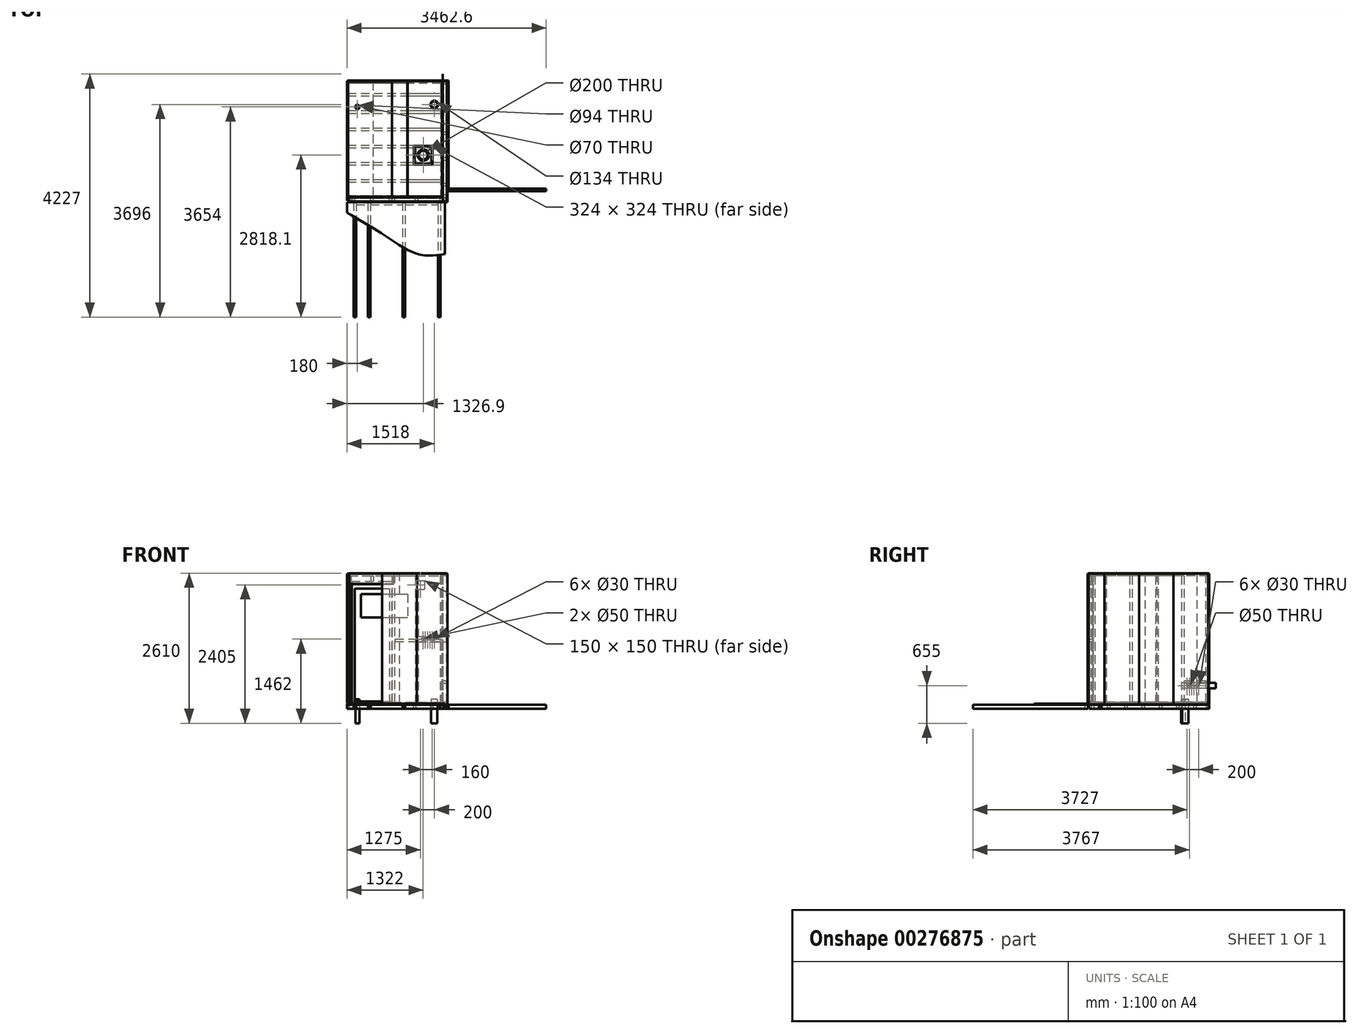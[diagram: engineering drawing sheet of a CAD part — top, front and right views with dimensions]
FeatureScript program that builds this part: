
annotation { "Feature Type Name" : "Feature", "Feature Type Description" : "" }
export const myFeature = defineFeature(function(context is Context, id is Id, definition is map)
    precondition{}
    {
        {
            var Q0;
            Q0=qCreatedBy(makeId("Front.planeOp"),FACE);
            cPlane(context, id + "F0", {"entities" : qUnion([Q0]), "cplaneType" : CPlaneType.OFFSET, "offset" : 15 * mm, "oppositeDirection" : true, "width" : 150 * mm, "height" : 150 * mm});
        }
        {
            var Q0;
            Q0=qCreatedBy(makeId("Right.planeOp"),FACE);
            cPlane(context, id + "F1", {"entities" : qUnion([Q0]), "cplaneType" : CPlaneType.OFFSET, "offset" : (15 + 20) * mm, "oppositeDirection" : true, "width" : 150 * mm, "height" : 150 * mm});
        }
        {
            var Q0;
            Q0=qCreatedBy(id+"F1.planeOp",FACE);
            cPlane(context, id + "F2", {"entities" : qUnion([Q0]), "cplaneType" : CPlaneType.OFFSET, "offset" : 1700 * mm, "width" : 150 * mm, "height" : 150 * mm});
        }
        {
            var Q0;
            Q0=qCreatedBy(id+"F0.planeOp",FACE);
            cPlane(context, id + "F3", {"entities" : qUnion([Q0]), "cplaneType" : CPlaneType.OFFSET, "offset" : 2069 * mm, "width" : 150 * mm, "height" : 150 * mm});
        }
        {
            var Q0;
            Q0=qCreatedBy(makeId("Top.planeOp"),FACE);
            cPlane(context, id + "F4", {"entities" : qUnion([Q0]), "cplaneType" : CPlaneType.OFFSET, "offset" : 0 * mm, "width" : 150 * mm, "height" : 150 * mm});
        }
        {
            var Q0;
            Q0=qCreatedBy(id+"F4.planeOp",FACE);
            var sketch = newSketch(context, id + "F5", { "sketchPlane" : qUnion([Q0])});
            skLineSegment(sketch, "E0.bottom", {"start": v(80, -2099) * mm, "end": v(125, -2099) * mm});
            skLineSegment(sketch, "E0.top", {"start": v(80, -4099) * mm, "end": v(125, -4099) * mm});
            skLineSegment(sketch, "E0.left", {"start": v(80, -2099) * mm, "end": v(80, -4099) * mm});
            skLineSegment(sketch, "E0.right", {"start": v(125, -2099) * mm, "end": v(125, -4099) * mm});
            skLineSegment(sketch, "E1.bottom", {"start": v(330, -2099) * mm, "end": v(375, -2099) * mm});
            skLineSegment(sketch, "E1.top", {"start": v(330, -4099) * mm, "end": v(375, -4099) * mm});
            skLineSegment(sketch, "E1.left", {"start": v(330, -2099) * mm, "end": v(330, -4099) * mm});
            skLineSegment(sketch, "E1.right", {"start": v(375, -2099) * mm, "end": v(375, -4099) * mm});
            skLineSegment(sketch, "E2.bottom", {"start": v(930, -2099) * mm, "end": v(975, -2099) * mm});
            skLineSegment(sketch, "E2.top", {"start": v(930, -4099) * mm, "end": v(975, -4099) * mm});
            skLineSegment(sketch, "E2.left", {"start": v(930, -2099) * mm, "end": v(930, -4099) * mm});
            skLineSegment(sketch, "E2.right", {"start": v(975, -2099) * mm, "end": v(975, -4099) * mm});
            skLineSegment(sketch, "E3.bottom", {"start": v(1545, -2099) * mm, "end": v(1590, -2099) * mm});
            skLineSegment(sketch, "E3.top", {"start": v(1545, -4099) * mm, "end": v(1590, -4099) * mm});
            skLineSegment(sketch, "E3.left", {"start": v(1545, -2099) * mm, "end": v(1545, -4099) * mm});
            skLineSegment(sketch, "E3.right", {"start": v(1590, -2099) * mm, "end": v(1590, -4099) * mm});
            skLineSegment(sketch, "E4.bottom", {"start": v(0, 0) * mm, "end": v(10, 0) * mm});
            skLineSegment(sketch, "E4.top", {"start": v(0, -10) * mm, "end": v(10, -10) * mm});
            skLineSegment(sketch, "E4.left", {"start": v(0, 0) * mm, "end": v(0, -10) * mm});
            skLineSegment(sketch, "E4.right", {"start": v(10, 0) * mm, "end": v(10, -10) * mm});
            skSolve(sketch);
        }
        {
            var Q0;
            Q0 = qSketchRegion(id + "F5", true);
            extrude(context, id + "F6", {"entities" : qUnion([Q0]), "oppositeDirection" : true, "depth" : 70 * mm});
        }
        {
            var Q0;
            Q0=qCreatedBy(id+"F4.planeOp",FACE);
            var sketch = newSketch(context, id + "F7", { "sketchPlane" : qUnion([Q0])});
            skLineSegment(sketch, "E5.bottom", {"start": v(-35, -2099) * mm, "end": v(1665, -2099) * mm});
            skLineSegment(sketch, "E5.left", {"start": v(-35, -2099) * mm, "end": v(-35, -2282.36) * mm});
            skLineSegment(sketch, "E5.right", {"start": v(1665, -2099) * mm, "end": v(1665, -3003.52) * mm});
            skFitSpline(sketch, "E6", {"points": [v(-35, -2282.36) * mm, v(571.63, -2645.47) * mm, v(1201.22, -3003.52) * mm, v(1665, -3003.52) * mm], "startDerivative": vector(1648.34, -970.88) * mm, "endDerivative": vector(1571.62, 233.74) * mm});
            skSolve(sketch);
        }
        {
            var Q0;
            Q0 = qSketchRegion(id + "F7", true);
            extrude(context, id + "F8", {"entities" : qUnion([Q0]), "depth" : 22 * mm});
        }
        {
            var Q0;
            Q0=qCreatedBy(id+"F4.planeOp",FACE);
            var sketch = newSketch(context, id + "F9", { "sketchPlane" : qUnion([Q0])});
            skLineSegment(sketch, "E7.bottom", {"start": v(1687.5, 15) * mm, "end": v(1642.5, 15) * mm});
            skLineSegment(sketch, "E7.top", {"start": v(1687.5, -2076.5) * mm, "end": v(1642.5, -2076.5) * mm});
            skLineSegment(sketch, "E7.left", {"start": v(1687.5, 15) * mm, "end": v(1687.5, -2076.5) * mm});
            skLineSegment(sketch, "E7.right", {"start": v(1642.5, 15) * mm, "end": v(1642.5, -2076.5) * mm});
            skLineSegment(sketch, "E8.bottom", {"start": v(-35, -2076.5) * mm, "end": v(1641.5, -2076.5) * mm});
            skLineSegment(sketch, "E8.top", {"start": v(-35, -2031.5) * mm, "end": v(1641.5, -2031.5) * mm});
            skLineSegment(sketch, "E8.left", {"start": v(-35, -2076.5) * mm, "end": v(-35, -2031.5) * mm});
            skLineSegment(sketch, "E8.right", {"start": v(1641.5, -2076.5) * mm, "end": v(1641.5, -2031.5) * mm});
            skPoint(sketch, "E9", {"position": v(1665, -2076.5) * mm});
            skPoint(sketch, "E10", {"position": v(1641.5, -2054) * mm});
            skLineSegment(sketch, "E11.bottom", {"start": v(126, -2099) * mm, "end": v(329, -2099) * mm});
            skLineSegment(sketch, "E11.top", {"start": v(126, -2144) * mm, "end": v(329, -2144) * mm});
            skLineSegment(sketch, "E11.left", {"start": v(126, -2099) * mm, "end": v(126, -2144) * mm});
            skLineSegment(sketch, "E11.right", {"start": v(329, -2099) * mm, "end": v(329, -2144) * mm});
            skLineSegment(sketch, "E12.bottom", {"start": v(376, -2099) * mm, "end": v(929, -2099) * mm});
            skLineSegment(sketch, "E12.top", {"start": v(376, -2144) * mm, "end": v(929, -2144) * mm});
            skLineSegment(sketch, "E12.left", {"start": v(376, -2099) * mm, "end": v(376, -2144) * mm});
            skLineSegment(sketch, "E12.right", {"start": v(929, -2099) * mm, "end": v(929, -2144) * mm});
            skLineSegment(sketch, "E13.bottom", {"start": v(976, -2099) * mm, "end": v(1544, -2099) * mm});
            skLineSegment(sketch, "E13.top", {"start": v(976, -2144) * mm, "end": v(1544, -2144) * mm});
            skLineSegment(sketch, "E13.left", {"start": v(976, -2099) * mm, "end": v(976, -2144) * mm});
            skLineSegment(sketch, "E13.right", {"start": v(1544, -2099) * mm, "end": v(1544, -2144) * mm});
            skLineSegment(sketch, "E14.bottom", {"start": v(1642.4, -2031.4) * mm, "end": v(1597.4, -2031.4) * mm});
            skLineSegment(sketch, "E14.top", {"start": v(1642.4, 15) * mm, "end": v(1597.4, 15) * mm});
            skLineSegment(sketch, "E14.left", {"start": v(1642.4, -2031.4) * mm, "end": v(1642.4, 15) * mm});
            skLineSegment(sketch, "E14.right", {"start": v(1597.4, -2031.4) * mm, "end": v(1597.4, 15) * mm});
            skLineSegment(sketch, "E15.bottom", {"start": v(-35, -1986.4) * mm, "end": v(1597.3, -1986.4) * mm});
            skLineSegment(sketch, "E15.top", {"start": v(-35, -2031.4) * mm, "end": v(1597.3, -2031.4) * mm});
            skLineSegment(sketch, "E15.left", {"start": v(-35, -1986.4) * mm, "end": v(-35, -2031.4) * mm});
            skLineSegment(sketch, "E15.right", {"start": v(1597.3, -1986.4) * mm, "end": v(1597.3, -2031.4) * mm});
            skLineSegment(sketch, "E16.bottom", {"start": v(1732.6, 15) * mm, "end": v(1687.6, 15) * mm});
            skLineSegment(sketch, "E16.top", {"start": v(1732.6, -1885) * mm, "end": v(1687.6, -1885) * mm});
            skLineSegment(sketch, "E16.left", {"start": v(1732.6, 15) * mm, "end": v(1732.6, -1885) * mm});
            skLineSegment(sketch, "E16.right", {"start": v(1687.6, 15) * mm, "end": v(1687.6, -1885) * mm});
            skLineSegment(sketch, "E17.bottom", {"start": v(1732.7, -1863) * mm, "end": v(3427.6, -1863) * mm});
            skLineSegment(sketch, "E17.top", {"start": v(1732.7, -1908) * mm, "end": v(3427.6, -1908) * mm});
            skLineSegment(sketch, "E17.left", {"start": v(1732.7, -1863) * mm, "end": v(1732.7, -1908) * mm});
            skLineSegment(sketch, "E17.right", {"start": v(3427.6, -1863) * mm, "end": v(3427.6, -1908) * mm});
            skSolve(sketch);
        }
        {
            var Q0;
            Q0 = qSketchRegion(id + "F9", true);
            extrude(context, id + "F10", {"entities" : qUnion([Q0]), "oppositeDirection" : true, "depth" : 70 * mm});
        }
        {
            var Q0;
            Q0=qCreatedBy(id+"F4.planeOp",FACE);
            var sketch = newSketch(context, id + "F11", { "sketchPlane" : qUnion([Q0])});
            skLineSegment(sketch, "E18.bottom", {"start": v(-25, -1708.4) * mm, "end": v(1596.4, -1708.4) * mm});
            skLineSegment(sketch, "E18.top", {"start": v(-25, -1753.4) * mm, "end": v(1596.4, -1753.4) * mm});
            skLineSegment(sketch, "E18.left", {"start": v(-25, -1708.4) * mm, "end": v(-25, -1753.4) * mm});
            skLineSegment(sketch, "E18.right", {"start": v(1596.4, -1708.4) * mm, "end": v(1596.4, -1753.4) * mm});
            skLineSegment(sketch, "E19.0.1.0", {"start": v(-25, -1408.4) * mm, "end": v(-25, -1453.4) * mm});
            skLineSegment(sketch, "E19.0.1.1", {"start": v(-25, -1408.4) * mm, "end": v(1596.4, -1408.4) * mm});
            skLineSegment(sketch, "E19.0.1.2", {"start": v(-25, -1453.4) * mm, "end": v(1596.4, -1453.4) * mm});
            skLineSegment(sketch, "E19.0.1.3", {"start": v(1596.4, -1408.4) * mm, "end": v(1596.4, -1453.4) * mm});
            skLineSegment(sketch, "E19.0.2.0", {"start": v(-25, -1108.4) * mm, "end": v(-25, -1153.4) * mm});
            skLineSegment(sketch, "E19.0.2.1", {"start": v(-25, -1108.4) * mm, "end": v(1596.4, -1108.4) * mm});
            skLineSegment(sketch, "E19.0.2.2", {"start": v(-25, -1153.4) * mm, "end": v(1596.4, -1153.4) * mm});
            skLineSegment(sketch, "E19.0.2.3", {"start": v(1596.4, -1108.4) * mm, "end": v(1596.4, -1153.4) * mm});
            skLineSegment(sketch, "E19.0.3.0", {"start": v(-25, -808.4) * mm, "end": v(-25, -853.4) * mm});
            skLineSegment(sketch, "E19.0.3.1", {"start": v(-25, -808.4) * mm, "end": v(1596.4, -808.4) * mm});
            skLineSegment(sketch, "E19.0.3.2", {"start": v(-25, -853.4) * mm, "end": v(1596.4, -853.4) * mm});
            skLineSegment(sketch, "E19.0.3.3", {"start": v(1596.4, -808.4) * mm, "end": v(1596.4, -853.4) * mm});
            skLineSegment(sketch, "E19.0.4.0", {"start": v(-25, -508.4) * mm, "end": v(-25, -553.4) * mm});
            skLineSegment(sketch, "E19.0.4.1", {"start": v(-25, -508.4) * mm, "end": v(1596.4, -508.4) * mm});
            skLineSegment(sketch, "E19.0.4.2", {"start": v(-25, -553.4) * mm, "end": v(1596.4, -553.4) * mm});
            skLineSegment(sketch, "E19.0.4.3", {"start": v(1596.4, -508.4) * mm, "end": v(1596.4, -553.4) * mm});
            skLineSegment(sketch, "E19.0.5.0", {"start": v(-25, -208.4) * mm, "end": v(-25, -253.4) * mm});
            skLineSegment(sketch, "E19.0.5.1", {"start": v(-25, -208.4) * mm, "end": v(1596.4, -208.4) * mm});
            skLineSegment(sketch, "E19.0.5.2", {"start": v(-25, -253.4) * mm, "end": v(1596.4, -253.4) * mm});
            skLineSegment(sketch, "E19.0.5.3", {"start": v(1596.4, -208.4) * mm, "end": v(1596.4, -253.4) * mm});
            skLineSegment(sketch, "E19.direction1", {"start": v(-25, -1753.4) * mm, "end": v(0, -1753.4) * mm, "construction": true});
            skLineSegment(sketch, "E19.direction2", {"start": v(-25, -1753.4) * mm, "end": v(-25, -1453.4) * mm, "construction": true});
            skLineSegment(sketch, "E20.bottom", {"start": v(1596.4, -35) * mm, "end": v(-25, -35) * mm});
            skLineSegment(sketch, "E20.top", {"start": v(1596.4, 10) * mm, "end": v(-25, 10) * mm});
            skLineSegment(sketch, "E20.left", {"start": v(1596.4, -35) * mm, "end": v(1596.4, 10) * mm});
            skLineSegment(sketch, "E20.right", {"start": v(-25, -35) * mm, "end": v(-25, 10) * mm});
            skLineSegment(sketch, "E21.bottom", {"start": v(1464.4, -1407.4) * mm, "end": v(1419.4, -1407.4) * mm});
            skLineSegment(sketch, "E21.top", {"start": v(1464.4, -1154.4) * mm, "end": v(1419.4, -1154.4) * mm});
            skLineSegment(sketch, "E21.left", {"start": v(1464.4, -1407.4) * mm, "end": v(1464.4, -1154.4) * mm});
            skLineSegment(sketch, "E21.right", {"start": v(1419.4, -1407.4) * mm, "end": v(1419.4, -1154.4) * mm});
            skLineSegment(sketch, "E22.bottom", {"start": v(1119.4, -1154.4) * mm, "end": v(1164.4, -1154.4) * mm});
            skLineSegment(sketch, "E22.top", {"start": v(1119.4, -1407.4) * mm, "end": v(1164.4, -1407.4) * mm});
            skLineSegment(sketch, "E22.left", {"start": v(1119.4, -1154.4) * mm, "end": v(1119.4, -1407.4) * mm});
            skLineSegment(sketch, "E22.right", {"start": v(1164.4, -1154.4) * mm, "end": v(1164.4, -1407.4) * mm});
            skSolve(sketch);
        }
        {
            var Q0;
            Q0 = qSketchRegion(id + "F11", true);
            extrude(context, id + "F12", {"entities" : qUnion([Q0]), "oppositeDirection" : true, "depth" : 70 * mm});
        }
        {
            var Q0;
            Q0=qCreatedBy(id+"F2.planeOp",FACE);
            var sketch = newSketch(context, id + "F13", { "sketchPlane" : qUnion([Q0])});
            skLineSegment(sketch, "E23.bottom", {"start": v(-2089, 0) * mm, "end": v(0, 0) * mm});
            skLineSegment(sketch, "E23.top", {"start": v(-2089, 45) * mm, "end": v(0, 45) * mm});
            skLineSegment(sketch, "E23.left", {"start": v(-2089, 0) * mm, "end": v(-2089, 45) * mm});
            skLineSegment(sketch, "E23.right", {"start": v(0, 0) * mm, "end": v(0, 45) * mm});
            skLineSegment(sketch, "E24.bottom", {"start": v(0, 46) * mm, "end": v(-45, 46) * mm});
            skLineSegment(sketch, "E24.top", {"start": v(0, 2244) * mm, "end": v(-45, 2244) * mm});
            skLineSegment(sketch, "E24.left", {"start": v(0, 46) * mm, "end": v(0, 2244) * mm});
            skLineSegment(sketch, "E24.right", {"start": v(-45, 46) * mm, "end": v(-45, 2244) * mm});
            skLineSegment(sketch, "E25.bottom", {"start": v(0, 2290) * mm, "end": v(-2089, 2290) * mm});
            skLineSegment(sketch, "E25.top", {"start": v(0, 2245) * mm, "end": v(-2089, 2245) * mm});
            skLineSegment(sketch, "E25.left", {"start": v(0, 2290) * mm, "end": v(0, 2245) * mm});
            skLineSegment(sketch, "E25.right", {"start": v(-2089, 2290) * mm, "end": v(-2089, 2245) * mm});
            skLineSegment(sketch, "E26.bottom", {"start": v(-2089, 2244) * mm, "end": v(-2044, 2244) * mm});
            skLineSegment(sketch, "E26.top", {"start": v(-2089, 46) * mm, "end": v(-2044, 46) * mm});
            skLineSegment(sketch, "E26.left", {"start": v(-2089, 2244) * mm, "end": v(-2089, 46) * mm});
            skLineSegment(sketch, "E26.right", {"start": v(-2044, 2244) * mm, "end": v(-2044, 46) * mm});
            skLineSegment(sketch, "E27.bottom", {"start": v(-428, 2244) * mm, "end": v(-473, 2244) * mm});
            skLineSegment(sketch, "E27.top", {"start": v(-428, 46) * mm, "end": v(-473, 46) * mm});
            skLineSegment(sketch, "E27.left", {"start": v(-428, 2244) * mm, "end": v(-428, 46) * mm});
            skLineSegment(sketch, "E27.right", {"start": v(-473, 2244) * mm, "end": v(-473, 46) * mm});
            skLineSegment(sketch, "E28.1.0.0", {"start": v(-923, 2244) * mm, "end": v(-923, 46) * mm});
            skLineSegment(sketch, "E28.1.0.1", {"start": v(-878, 2244) * mm, "end": v(-923, 2244) * mm});
            skLineSegment(sketch, "E28.1.0.2", {"start": v(-878, 2244) * mm, "end": v(-878, 46) * mm});
            skLineSegment(sketch, "E28.1.0.3", {"start": v(-878, 46) * mm, "end": v(-923, 46) * mm});
            skLineSegment(sketch, "E28.2.0.0", {"start": v(-1373, 2244) * mm, "end": v(-1373, 46) * mm});
            skLineSegment(sketch, "E28.2.0.1", {"start": v(-1328, 2244) * mm, "end": v(-1373, 2244) * mm});
            skLineSegment(sketch, "E28.2.0.2", {"start": v(-1328, 2244) * mm, "end": v(-1328, 46) * mm});
            skLineSegment(sketch, "E28.2.0.3", {"start": v(-1328, 46) * mm, "end": v(-1373, 46) * mm});
            skLineSegment(sketch, "E28.direction1", {"start": v(-473, 46) * mm, "end": v(-923, 46) * mm, "construction": true});
            skLineSegment(sketch, "E29.bottom", {"start": v(-46, 415) * mm, "end": v(-427, 415) * mm});
            skLineSegment(sketch, "E29.top", {"start": v(-46, 370) * mm, "end": v(-427, 370) * mm});
            skLineSegment(sketch, "E29.left", {"start": v(-46, 415) * mm, "end": v(-46, 370) * mm});
            skLineSegment(sketch, "E29.right", {"start": v(-427, 415) * mm, "end": v(-427, 370) * mm});
            skLineSegment(sketch, "E30.bottom", {"start": v(-924, 1190) * mm, "end": v(-1327, 1190) * mm, "construction": true});
            skLineSegment(sketch, "E30.top", {"start": v(-924, 1145) * mm, "end": v(-1327, 1145) * mm, "construction": true});
            skLineSegment(sketch, "E30.left", {"start": v(-924, 1190) * mm, "end": v(-924, 1145) * mm});
            skLineSegment(sketch, "E30.right", {"start": v(-1327, 1190) * mm, "end": v(-1327, 1145) * mm});
            skLineSegment(sketch, "E31.bottom", {"start": v(-877, 1190) * mm, "end": v(-474, 1190) * mm, "construction": true});
            skLineSegment(sketch, "E31.top", {"start": v(-877, 1145) * mm, "end": v(-474, 1145) * mm, "construction": true});
            skLineSegment(sketch, "E31.left", {"start": v(-877, 1190) * mm, "end": v(-877, 1145) * mm});
            skLineSegment(sketch, "E31.right", {"start": v(-474, 1190) * mm, "end": v(-474, 1145) * mm});
            skLineSegment(sketch, "E32.bottom", {"start": v(-427, 1190) * mm, "end": v(-46, 1190) * mm, "construction": true});
            skLineSegment(sketch, "E32.top", {"start": v(-427, 1145) * mm, "end": v(-46, 1145) * mm, "construction": true});
            skLineSegment(sketch, "E32.left", {"start": v(-427, 1190) * mm, "end": v(-427, 1145) * mm});
            skLineSegment(sketch, "E32.right", {"start": v(-46, 1190) * mm, "end": v(-46, 1145) * mm});
            skLineSegment(sketch, "E33.bottom", {"start": v(-1374, 1190) * mm, "end": v(-1777, 1190) * mm, "construction": true});
            skLineSegment(sketch, "E33.top", {"start": v(-1374, 1145) * mm, "end": v(-1777, 1145) * mm, "construction": true});
            skLineSegment(sketch, "E33.left", {"start": v(-1374, 1190) * mm, "end": v(-1374, 1145) * mm});
            skLineSegment(sketch, "E33.right", {"start": v(-1777, 1190) * mm, "end": v(-1777, 1145) * mm});
            skLineSegment(sketch, "E34.0.3.0", {"start": v(-1823, 2244) * mm, "end": v(-1823, 46) * mm});
            skLineSegment(sketch, "E34.3.3.0", {"start": v(-1778, 2244) * mm, "end": v(-1823, 2244) * mm});
            skLineSegment(sketch, "E34.6.3.0", {"start": v(-1778, 2244) * mm, "end": v(-1778, 46) * mm});
            skLineSegment(sketch, "E34.9.3.0", {"start": v(-1778, 46) * mm, "end": v(-1823, 46) * mm});
            skLineSegment(sketch, "E35.bottom", {"start": v(-2019, 2244) * mm, "end": v(-1974, 2244) * mm});
            skLineSegment(sketch, "E35.top", {"start": v(-2019, 46) * mm, "end": v(-1974, 46) * mm});
            skLineSegment(sketch, "E35.left", {"start": v(-2019, 2244) * mm, "end": v(-2019, 46) * mm});
            skLineSegment(sketch, "E35.right", {"start": v(-1974, 2244) * mm, "end": v(-1974, 46) * mm});
            skSolve(sketch);
        }
        {
            var Q0;
            Q0 = qSketchRegion(id + "F13", true);
            extrude(context, id + "F14", {"entities" : qUnion([Q0]), "endBound" : BoundingType.SYMMETRIC, "depth" : 70 * mm});
        }
        {
            var Q0;
            Q0=qCreatedBy(id+"F3.planeOp",FACE);
            var sketch = newSketch(context, id + "F15", { "sketchPlane" : qUnion([Q0])});
            skLineSegment(sketch, "E36.bottom", {"start": v(755, 0) * mm, "end": v(1630, 0) * mm});
            skLineSegment(sketch, "E36.top", {"start": v(755, 45) * mm, "end": v(1630, 45) * mm});
            skLineSegment(sketch, "E36.left", {"start": v(755, 0) * mm, "end": v(755, 45) * mm});
            skLineSegment(sketch, "E36.right", {"start": v(1630, 0) * mm, "end": v(1630, 45) * mm});
            skLineSegment(sketch, "E37.bottom", {"start": v(755, 46) * mm, "end": v(800, 46) * mm});
            skLineSegment(sketch, "E37.top", {"start": v(755, 2244) * mm, "end": v(800, 2244) * mm});
            skLineSegment(sketch, "E37.left", {"start": v(755, 46) * mm, "end": v(755, 2244) * mm});
            skLineSegment(sketch, "E37.right", {"start": v(800, 46) * mm, "end": v(800, 2244) * mm});
            skLineSegment(sketch, "E38.bottom", {"start": v(0, 2290) * mm, "end": v(1630, 2290) * mm});
            skLineSegment(sketch, "E38.top", {"start": v(0, 2245) * mm, "end": v(1630, 2245) * mm});
            skLineSegment(sketch, "E38.left", {"start": v(0, 2290) * mm, "end": v(0, 2245) * mm});
            skLineSegment(sketch, "E38.right", {"start": v(1630, 2290) * mm, "end": v(1630, 2245) * mm});
            skLineSegment(sketch, "E39.bottom", {"start": v(0, 0) * mm, "end": v(45, 0) * mm});
            skLineSegment(sketch, "E39.top", {"start": v(0, 2244) * mm, "end": v(45, 2244) * mm});
            skLineSegment(sketch, "E39.left", {"start": v(0, 0) * mm, "end": v(0, 2244) * mm});
            skLineSegment(sketch, "E39.right", {"start": v(45, 0) * mm, "end": v(45, 2244) * mm});
            skLineSegment(sketch, "E40.bottom", {"start": v(46, 2145) * mm, "end": v(754, 2145) * mm});
            skLineSegment(sketch, "E40.top", {"start": v(46, 2100) * mm, "end": v(754, 2100) * mm});
            skLineSegment(sketch, "E40.left", {"start": v(46, 2145) * mm, "end": v(46, 2100) * mm});
            skLineSegment(sketch, "E40.right", {"start": v(754, 2145) * mm, "end": v(754, 2100) * mm});
            skLineSegment(sketch, "E41.bottom", {"start": v(1157, 2244) * mm, "end": v(1202, 2244) * mm});
            skLineSegment(sketch, "E41.top", {"start": v(1157, 46) * mm, "end": v(1202, 46) * mm});
            skLineSegment(sketch, "E41.left", {"start": v(1157, 2244) * mm, "end": v(1157, 46) * mm});
            skLineSegment(sketch, "E41.right", {"start": v(1202, 2244) * mm, "end": v(1202, 46) * mm});
            skLineSegment(sketch, "E42.bottom", {"start": v(1203, 1145) * mm, "end": v(1584, 1145) * mm});
            skLineSegment(sketch, "E42.top", {"start": v(1203, 1100) * mm, "end": v(1584, 1100) * mm});
            skLineSegment(sketch, "E42.left", {"start": v(1203, 1145) * mm, "end": v(1203, 1100) * mm});
            skLineSegment(sketch, "E42.right", {"start": v(1584, 1145) * mm, "end": v(1584, 1100) * mm});
            skLineSegment(sketch, "E43.bottom", {"start": v(801, 1145) * mm, "end": v(1156, 1145) * mm});
            skLineSegment(sketch, "E43.top", {"start": v(801, 1100) * mm, "end": v(1156, 1100) * mm});
            skLineSegment(sketch, "E43.left", {"start": v(801, 1145) * mm, "end": v(801, 1100) * mm});
            skLineSegment(sketch, "E43.right", {"start": v(1156, 1145) * mm, "end": v(1156, 1100) * mm});
            skLineSegment(sketch, "E44.bottom", {"start": v(377.5, 2244) * mm, "end": v(422.5, 2244) * mm});
            skLineSegment(sketch, "E44.top", {"start": v(377.5, 2146) * mm, "end": v(422.5, 2146) * mm});
            skLineSegment(sketch, "E44.left", {"start": v(377.5, 2244) * mm, "end": v(377.5, 2146) * mm});
            skLineSegment(sketch, "E44.right", {"start": v(422.5, 2244) * mm, "end": v(422.5, 2146) * mm});
            skLineSegment(sketch, "E45", {"start": v(400, 2244) * mm, "end": v(400, 2146.44) * mm, "construction": true});
            skLineSegment(sketch, "E46.bottom", {"start": v(1630, 2244) * mm, "end": v(1585, 2244) * mm});
            skLineSegment(sketch, "E46.top", {"start": v(1630, 46) * mm, "end": v(1585, 46) * mm});
            skLineSegment(sketch, "E46.left", {"start": v(1630, 2244) * mm, "end": v(1630, 46) * mm});
            skLineSegment(sketch, "E46.right", {"start": v(1585, 2244) * mm, "end": v(1585, 46) * mm});
            skSolve(sketch);
        }
        {
            var Q0;
            Q0 = qSketchRegion(id + "F15", true);
            extrude(context, id + "F16", {"entities" : qUnion([Q0]), "endBound" : BoundingType.SYMMETRIC, "depth" : 70 * mm});
        }
        {
            var Q0;
            Q0=qCreatedBy(id+"F3.planeOp",FACE);
            var sketch = newSketch(context, id + "F17", { "sketchPlane" : qUnion([Q0])});
            skLineSegment(sketch, "E47", {"start": v(50, 25) * mm, "end": v(97.5, 25) * mm});
            skLineSegment(sketch, "E48", {"start": v(97.5, 25) * mm, "end": v(97.5, 2020) * mm});
            skLineSegment(sketch, "E49", {"start": v(97.5, 2020) * mm, "end": v(702.5, 2020) * mm});
            skLineSegment(sketch, "E50", {"start": v(702.5, 2020) * mm, "end": v(702.5, 25) * mm});
            skLineSegment(sketch, "E51", {"start": v(702.5, 25) * mm, "end": v(750, 25) * mm});
            skLineSegment(sketch, "E52", {"start": v(750, 25) * mm, "end": v(750, 2095) * mm});
            skLineSegment(sketch, "E53", {"start": v(750, 2095) * mm, "end": v(50, 2095) * mm});
            skLineSegment(sketch, "E54", {"start": v(50, 2095) * mm, "end": v(50, 25) * mm});
            skSolve(sketch);
        }
        {
            var Q0;
            Q0 = qSketchRegion(id + "F17", true);
            extrude(context, id + "F18", {"entities" : qUnion([Q0]), "endBound" : BoundingType.SYMMETRIC, "depth" : 90 * mm});
        }
        {
            var Q0;
            Q0=makeQuery(id+"F16.opExtrude","CAP_FACE",FACE,{"disambiguationData":[OSD([sQuery(id+"F15.wireOp",EDGE,"E36.bottom"),sQuery(id+"F15.wireOp",EDGE,"E36.top"),sQuery(id+"F15.wireOp",EDGE,"E36.left"),sQuery(id+"F15.wireOp",EDGE,"E36.right")])],"isStart":true});
            var sketch = newSketch(context, id + "F19", { "sketchPlane" : qUnion([Q0])});
            skLineSegment(sketch, "E55.bottom", {"start": v(-1187, 1192) * mm, "end": v(-1687, 1192) * mm});
            skLineSegment(sketch, "E55.top", {"start": v(-1187, 1092) * mm, "end": v(-1687, 1092) * mm});
            skLineSegment(sketch, "E55.left", {"start": v(-1187, 1192) * mm, "end": v(-1187, 1092) * mm});
            skLineSegment(sketch, "E55.right", {"start": v(-1687, 1192) * mm, "end": v(-1687, 1092) * mm});
            skCircle(sketch, "E56", {"center": v(-1287, 1142) * mm, "radius": 15 * mm});
            skCircle(sketch, "E57.1.0.0", {"center": v(-1327, 1142) * mm, "radius": 15 * mm});
            skCircle(sketch, "E57.2.0.0", {"center": v(-1367, 1142) * mm, "radius": 15 * mm});
            skLineSegment(sketch, "E57.direction1", {"start": v(-1287, 1142) * mm, "end": v(-1327, 1142) * mm, "construction": true});
            skCircle(sketch, "E58.0.3.0", {"center": v(-1407, 1142) * mm, "radius": 15 * mm});
            skCircle(sketch, "E58.0.4.0", {"center": v(-1447, 1142) * mm, "radius": 15 * mm});
            skCircle(sketch, "E58.0.5.0", {"center": v(-1487, 1142) * mm, "radius": 15 * mm});
            skSolve(sketch);
        }
        {
            var Q0;
            Q0=makeQuery(id+"F19.imprint","IMPRINT",FACE,{"disambiguationData":[TD([[makeQuery(id+"F19.imprint","IMPRINT",EDGE,{"derivedFrom":sQuery(id+"F19.wireOp",EDGE,"E55.bottom")}),1.0]])]});
            extrude(context, id + "F20", {"entities" : qUnion([Q0]), "depth" : 1 * mm});
        }
        {
            var Q0;
            Q0=makeQuery(id+"F14.opExtrude","CAP_FACE",FACE,{"disambiguationData":[OSD([sQuery(id+"F13.wireOp",EDGE,"E23.bottom"),sQuery(id+"F13.wireOp",EDGE,"E23.top"),sQuery(id+"F13.wireOp",EDGE,"E23.left"),sQuery(id+"F13.wireOp",EDGE,"E23.right")])],"isStart":true});
            var sketch = newSketch(context, id + "F21", { "sketchPlane" : qUnion([Q0])});
            skLineSegment(sketch, "E59.bottom", {"start": v(-128, 385) * mm, "end": v(472, 385) * mm});
            skLineSegment(sketch, "E59.top", {"start": v(-128, 285) * mm, "end": v(472, 285) * mm});
            skLineSegment(sketch, "E59.left", {"start": v(-128, 385) * mm, "end": v(-128, 285) * mm});
            skLineSegment(sketch, "E59.right", {"start": v(472, 385) * mm, "end": v(472, 285) * mm});
            skCircle(sketch, "E60", {"center": v(372, 335) * mm, "radius": 15 * mm});
            skCircle(sketch, "E61.1.0.0", {"center": v(332, 335) * mm, "radius": 15 * mm});
            skCircle(sketch, "E61.2.0.0", {"center": v(292, 335) * mm, "radius": 15 * mm});
            skLineSegment(sketch, "E61.direction1", {"start": v(372, 335) * mm, "end": v(332, 335) * mm, "construction": true});
            skCircle(sketch, "E62.0.3.0", {"center": v(252, 335) * mm, "radius": 15 * mm});
            skCircle(sketch, "E62.0.4.0", {"center": v(212, 335) * mm, "radius": 15 * mm});
            skCircle(sketch, "E62.0.5.0", {"center": v(172, 335) * mm, "radius": 15 * mm});
            skSolve(sketch);
        }
        {
            var Q0;
            Q0 = qSketchRegion(id + "F21", true);
            extrude(context, id + "F22", {"entities" : qUnion([Q0]), "depth" : 1 * mm});
        }
        {
            var Q0;
            Q0=qCreatedBy(id+"F4.planeOp",FACE);
            var sketch = newSketch(context, id + "F23", { "sketchPlane" : qUnion([Q0])});
            skCircle(sketch, "E63", {"center": v(1291.9, -1280.9) * mm, "radius": 100 * mm});
            skLineSegment(sketch, "E64.bottom", {"start": v(1441.9, -1130.9) * mm, "end": v(1141.9, -1130.9) * mm});
            skLineSegment(sketch, "E64.top", {"start": v(1441.9, -1430.9) * mm, "end": v(1141.9, -1430.9) * mm});
            skLineSegment(sketch, "E64.left", {"start": v(1441.9, -1130.9) * mm, "end": v(1441.9, -1430.9) * mm});
            skLineSegment(sketch, "E64.right", {"start": v(1141.9, -1130.9) * mm, "end": v(1141.9, -1430.9) * mm});
            skLineSegment(sketch, "E65", {"start": v(1291.9, -1280.9) * mm, "end": v(1164.4, -1280.9) * mm, "construction": true});
            skLineSegment(sketch, "E66", {"start": v(1291.9, -1280.9) * mm, "end": v(1419.4, -1280.9) * mm, "construction": true});
            skCircle(sketch, "E67", {"center": v(1291.9, -1280.9) * mm, "radius": 75 * mm});
            skLineSegment(sketch, "E68", {"start": v(1612, -1226.59) * mm, "end": v(1612, -1307.19) * mm, "construction": true});
            skPoint(sketch, "E69", {"position": v(1366.9, -1280.9) * mm});
            skPoint(sketch, "E70", {"position": v(1291.9, -1205.9) * mm});
            skSolve(sketch);
        }
        {
            var Q0;
            Q0=makeQuery(id+"F23.imprint","IMPRINT",FACE,{"disambiguationData":[TD([[makeQuery(id+"F23.imprint","IMPRINT",EDGE,{"derivedFrom":sQuery(id+"F23.wireOp",EDGE,"E63")}),-1.0]])]});
            var Q1;
            Q1=makeQuery(id+"F23.imprint","IMPRINT",FACE,{"disambiguationData":[TD([[makeQuery(id+"F23.imprint","IMPRINT",EDGE,{"derivedFrom":sQuery(id+"F23.wireOp",EDGE,"E67")}),1.0]])]});
            extrude(context, id + "F24", {"entities" : qUnion([Q0, Q1]), "depth" : (22 + 13) * mm});
        }
        {
            var Q0;
            Q0=qCreatedBy(id+"F4.planeOp",FACE);
            var sketch = newSketch(context, id + "F25", { "sketchPlane" : qUnion([Q0])});
            skCircle(sketch, "E71", {"center": v(1483, -403) * mm, "radius": 55 * mm});
            skSolve(sketch);
        }
        {
            var Q0;
            Q0 = qSketchRegion(id + "F25", true);
            extrude(context, id + "F26", {"entities" : qUnion([Q0]), "depth" : (22 + 33 + 5 + 40) * mm, "hasSecondDirection" : true, "secondDirectionOppositeDirection" : true, "secondDirectionDepth" : (70 + 150 + 100) * mm});
        }
        {
            var Q0;
            Q0=qCreatedBy(id+"F4.planeOp",FACE);
            var sketch = newSketch(context, id + "F27", { "sketchPlane" : qUnion([Q0])});
            skCircle(sketch, "E72", {"center": v(145, -445) * mm, "radius": 35 * mm});
            skSolve(sketch);
        }
        {
            var Q0;
            Q0 = qSketchRegion(id + "F27", true);
            extrude(context, id + "F28", {"entities" : qUnion([Q0]), "depth" : (22 + 33 + 5 + 40) * mm, "hasSecondDirection" : true, "secondDirectionOppositeDirection" : true, "secondDirectionDepth" : (70 + 150 + 100) * mm});
        }
        {
            var Q0;
            Q0=qCreatedBy(id+"F4.planeOp",FACE);
            var sketch = newSketch(context, id + "F29", { "sketchPlane" : qUnion([Q0])});
            skLineSegment(sketch, "E73.bottom", {"start": v(-23, 3) * mm, "end": v(416, 3) * mm});
            skLineSegment(sketch, "E73.top", {"start": v(-23, -2007) * mm, "end": v(57, -2007) * mm});
            skLineSegment(sketch, "E73.left", {"start": v(-23, 3) * mm, "end": v(-23, -2007) * mm});
            skLineSegment(sketch, "E73.right", {"start": v(416, 3) * mm, "end": v(416, -2089) * mm});
            skLineSegment(sketch, "E74", {"start": v(57, -2007) * mm, "end": v(57, -2089) * mm});
            skLineSegment(sketch, "E75", {"start": v(57, -2089) * mm, "end": v(416, -2089) * mm});
            skLineSegment(sketch, "E76.bottom", {"start": v(1017, 3) * mm, "end": v(417, 3) * mm});
            skLineSegment(sketch, "E76.top", {"start": v(1017, -2007) * mm, "end": v(743, -2007) * mm});
            skLineSegment(sketch, "E76.left", {"start": v(1017, 3) * mm, "end": v(1017, -2007) * mm});
            skLineSegment(sketch, "E76.right", {"start": v(417, 3) * mm, "end": v(417, -2089) * mm});
            skLineSegment(sketch, "E77", {"start": v(743, -2007) * mm, "end": v(743, -2089) * mm});
            skLineSegment(sketch, "E78", {"start": v(743, -2089) * mm, "end": v(417, -2089) * mm});
            skLineSegment(sketch, "E79.bottom", {"start": v(1018, 3) * mm, "end": v(1618, 3) * mm});
            skLineSegment(sketch, "E79.top", {"start": v(1018, -2007) * mm, "end": v(1618, -2007) * mm});
            skLineSegment(sketch, "E79.left", {"start": v(1018, 3) * mm, "end": v(1018, -2007) * mm});
            skLineSegment(sketch, "E79.right", {"start": v(1618, 3) * mm, "end": v(1618, -2007) * mm});
            skLineSegment(sketch, "E80.bottom", {"start": v(1453.9, -1442.9) * mm, "end": v(1129.9, -1442.9) * mm});
            skLineSegment(sketch, "E80.top", {"start": v(1453.9, -1118.9) * mm, "end": v(1129.9, -1118.9) * mm});
            skLineSegment(sketch, "E80.left", {"start": v(1453.9, -1442.9) * mm, "end": v(1453.9, -1118.9) * mm});
            skLineSegment(sketch, "E80.right", {"start": v(1129.9, -1442.9) * mm, "end": v(1129.9, -1118.9) * mm});
            skPoint(sketch, "E80.middle", {"position": v(1291.9, -1280.9) * mm});
            skCircle(sketch, "E81", {"center": v(1483, -403) * mm, "radius": 67 * mm});
            skCircle(sketch, "E82", {"center": v(145, -445) * mm, "radius": 47 * mm});
            skSolve(sketch);
        }
        {
            var Q0;
            Q0 = qSketchRegion(id + "F29", true);
            extrude(context, id + "F30", {"entities" : qUnion([Q0]), "depth" : 22 * mm});
        }
        {
            var Q0;
            Q0=makeQuery(id+"F14.opExtrude","CAP_FACE",FACE,{"disambiguationData":[OSD([sQuery(id+"F13.wireOp",EDGE,"E23.bottom"),sQuery(id+"F13.wireOp",EDGE,"E23.top"),sQuery(id+"F13.wireOp",EDGE,"E23.left"),sQuery(id+"F13.wireOp",EDGE,"E23.right")])],"isStart":true});
            var sketch = newSketch(context, id + "F31", { "sketchPlane" : qUnion([Q0])});
            skLineSegment(sketch, "E83.bottom", {"start": v(5, 2285) * mm, "end": v(905, 2285) * mm});
            skLineSegment(sketch, "E83.top", {"start": v(5, 27) * mm, "end": v(905, 27) * mm});
            skLineSegment(sketch, "E83.left", {"start": v(5, 2285) * mm, "end": v(5, 27) * mm});
            skLineSegment(sketch, "E83.right", {"start": v(905, 2285) * mm, "end": v(905, 27) * mm});
            skLineSegment(sketch, "E84.bottom", {"start": v(906, 2285) * mm, "end": v(1806, 2285) * mm});
            skLineSegment(sketch, "E84.top", {"start": v(906, 27) * mm, "end": v(1806, 27) * mm});
            skLineSegment(sketch, "E84.left", {"start": v(906, 2285) * mm, "end": v(906, 27) * mm});
            skLineSegment(sketch, "E84.right", {"start": v(1806, 2285) * mm, "end": v(1806, 27) * mm});
            skLineSegment(sketch, "E85.bottom", {"start": v(1807, 2285) * mm, "end": v(2014, 2285) * mm});
            skLineSegment(sketch, "E85.top", {"start": v(1807, 27) * mm, "end": v(2014, 27) * mm});
            skLineSegment(sketch, "E85.left", {"start": v(1807, 2285) * mm, "end": v(1807, 27) * mm});
            skLineSegment(sketch, "E85.right", {"start": v(2014, 2285) * mm, "end": v(2014, 27) * mm});
            skCircle(sketch, "E86", {"center": v(332, 335) * mm, "radius": 25 * mm});
            skSolve(sketch);
        }
        {
            var Q0;
            Q0 = qSketchRegion(id + "F31", true);
            extrude(context, id + "F32", {"entities" : qUnion([Q0]), "depth" : 12.5 * mm});
        }
        {
            var Q0;
            Q0=makeQuery(id+"F16.opExtrude","CAP_FACE",FACE,{"disambiguationData":[OSD([sQuery(id+"F15.wireOp",EDGE,"E36.bottom"),sQuery(id+"F15.wireOp",EDGE,"E36.top"),sQuery(id+"F15.wireOp",EDGE,"E36.left"),sQuery(id+"F15.wireOp",EDGE,"E36.right")])],"isStart":true});
            var sketch = newSketch(context, id + "F33", { "sketchPlane" : qUnion([Q0])});
            skLineSegment(sketch, "E87.bottom", {"start": v(-1612.5, 27) * mm, "end": v(-755, 27) * mm});
            skLineSegment(sketch, "E87.top", {"start": v(-1612.5, 2285) * mm, "end": v(-778, 2285) * mm});
            skLineSegment(sketch, "E87.left", {"start": v(-1612.5, 27) * mm, "end": v(-1612.5, 2285) * mm});
            skLineSegment(sketch, "E87.right", {"start": v(-778, 2100) * mm, "end": v(-778, 2285) * mm});
            skLineSegment(sketch, "E88", {"start": v(-755, 2100) * mm, "end": v(-778, 2100) * mm});
            skLineSegment(sketch, "E89", {"start": v(-755, 2100) * mm, "end": v(-755, 27) * mm});
            skLineSegment(sketch, "E90.bottom", {"start": v(-777, 2285) * mm, "end": v(-5, 2285) * mm});
            skLineSegment(sketch, "E90.top", {"start": v(-777, 2101) * mm, "end": v(-5, 2101) * mm});
            skLineSegment(sketch, "E90.left", {"start": v(-777, 2285) * mm, "end": v(-777, 2101) * mm});
            skLineSegment(sketch, "E90.right", {"start": v(-5, 2285) * mm, "end": v(-5, 2101) * mm});
            skLineSegment(sketch, "E91.bottom", {"start": v(-45, 2100) * mm, "end": v(-5, 2100) * mm});
            skLineSegment(sketch, "E91.top", {"start": v(-45, 27) * mm, "end": v(-5, 27) * mm});
            skLineSegment(sketch, "E91.left", {"start": v(-45, 2100) * mm, "end": v(-45, 27) * mm});
            skLineSegment(sketch, "E91.right", {"start": v(-5, 2100) * mm, "end": v(-5, 27) * mm});
            skCircle(sketch, "E92", {"center": v(-1447, 1142) * mm, "radius": 25 * mm});
            skCircle(sketch, "E93", {"center": v(-1287, 1142) * mm, "radius": 25 * mm});
            skSolve(sketch);
        }
        {
            var Q0;
            Q0 = qSketchRegion(id + "F33", true);
            extrude(context, id + "F34", {"entities" : qUnion([Q0]), "depth" : 12.5 * mm});
        }
        {
            var Q0;
            Q0=makeQuery(id+"F30.opExtrude","CAP_FACE",FACE,{"disambiguationData":[OSD([sQuery(id+"F29.wireOp",EDGE,"E79.bottom"),sQuery(id+"F29.wireOp",EDGE,"E79.top"),sQuery(id+"F29.wireOp",EDGE,"E79.left"),sQuery(id+"F29.wireOp",EDGE,"E79.right"),sQuery(id+"F29.wireOp",EDGE,"E80.bottom"),sQuery(id+"F29.wireOp",EDGE,"E80.top"),sQuery(id+"F29.wireOp",EDGE,"E80.left"),sQuery(id+"F29.wireOp",EDGE,"E80.right"),sQuery(id+"F29.wireOp",EDGE,"E81")])],"isStart":false});
            var sketch = newSketch(context, id + "F35", { "sketchPlane" : qUnion([Q0])});
            skLineSegment(sketch, "E94", {"start": v(745, -6.3) * mm, "end": v(-11.62, -6.3) * mm});
            skLineSegment(sketch, "E95", {"start": v(-11.62, -6.3) * mm, "end": v(-11.62, -2006.5) * mm});
            skLineSegment(sketch, "E96", {"start": v(-11.62, -2006.5) * mm, "end": v(745, -2006.5) * mm});
            skLineSegment(sketch, "E97", {"start": v(745, -2006.5) * mm, "end": v(745, -6.3) * mm});
            skCircle(sketch, "E98.0.0", {"center": v(145, -445) * mm, "radius": 35 * mm});
            skSolve(sketch);
        }
        {
            var Q0;
            Q0 = qSketchRegion(id + "F35", true);
            extrude(context, id + "F36", {"entities" : qUnion([Q0]), "depth" : 33 * mm});
        }
        {
            var Q0;
            Q0=makeQuery(id+"F18.opExtrude","SWEPT_FACE",FACE,{"disambiguationData":[OSD([sQuery(id+"F17.wireOp",EDGE,"E50")])]});
            var sketch = newSketch(context, id + "F37", { "sketchPlane" : qUnion([Q0])});
            skLineSegment(sketch, "E99.bottom", {"start": v(2009, 57) * mm, "end": v(2099, 57) * mm});
            skLineSegment(sketch, "E99.top", {"start": v(2009, 22) * mm, "end": v(2099, 22) * mm});
            skLineSegment(sketch, "E99.left", {"start": v(2009, 57) * mm, "end": v(2009, 22) * mm});
            skLineSegment(sketch, "E99.right", {"start": v(2099, 57) * mm, "end": v(2099, 22) * mm});
            skSolve(sketch);
        }
        {
            var Q0;
            Q0 = qSketchRegion(id + "F37", true);
            var Q1;
            Q1=makeQuery(id+"F18.opExtrude","SWEPT_FACE",FACE,{"disambiguationData":[OSD([sQuery(id+"F17.wireOp",EDGE,"E48")])]});
            extrude(context, id + "F38", {"entities" : qUnion([Q0]), "endBound" : BoundingType.UP_TO_SURFACE, "endBoundEntityFace" : qUnion([Q1]), "depth" : 25 * mm});
        }
        {
            var Q0;
            Q0=qCreatedBy(id+"F1.planeOp",FACE);
            var sketch = newSketch(context, id + "F39", { "sketchPlane" : qUnion([Q0])});
            skLineSegment(sketch, "E100.bottom", {"start": v(-1104, 2280) * mm, "end": v(-2004, 2280) * mm});
            skLineSegment(sketch, "E100.top", {"start": v(-1104, 32) * mm, "end": v(-2004, 32) * mm});
            skLineSegment(sketch, "E100.left", {"start": v(-1104, 2280) * mm, "end": v(-1104, 32) * mm});
            skLineSegment(sketch, "E100.right", {"start": v(-2004, 2280) * mm, "end": v(-2004, 32) * mm});
            skLineSegment(sketch, "E101.bottom", {"start": v(-1103, 2280) * mm, "end": v(-203, 2280) * mm});
            skLineSegment(sketch, "E101.top", {"start": v(-1103, 32) * mm, "end": v(-203, 32) * mm});
            skLineSegment(sketch, "E101.left", {"start": v(-1103, 2280) * mm, "end": v(-1103, 32) * mm});
            skLineSegment(sketch, "E101.right", {"start": v(-203, 2280) * mm, "end": v(-203, 32) * mm});
            skLineSegment(sketch, "E102.bottom", {"start": v(-202, 2280) * mm, "end": v(10, 2280) * mm});
            skLineSegment(sketch, "E102.top", {"start": v(-202, 32) * mm, "end": v(10, 32) * mm});
            skLineSegment(sketch, "E102.left", {"start": v(-202, 2280) * mm, "end": v(-202, 32) * mm});
            skLineSegment(sketch, "E102.right", {"start": v(10, 2280) * mm, "end": v(10, 32) * mm});
            skSolve(sketch);
        }
        {
            var Q0;
            Q0 = qSketchRegion(id + "F39", true);
            extrude(context, id + "F40", {"entities" : qUnion([Q0]), "depth" : 15 * mm});
        }
        {
            var Q0;
            Q0=qCreatedBy(id+"F0.planeOp",FACE);
            var sketch = newSketch(context, id + "F41", { "sketchPlane" : qUnion([Q0])});
            skLineSegment(sketch, "E103.bottom", {"start": v(1612.5, 22) * mm, "end": v(880.1, 22) * mm});
            skLineSegment(sketch, "E103.top", {"start": v(1612.5, 2280) * mm, "end": v(880.1, 2280) * mm});
            skLineSegment(sketch, "E103.left", {"start": v(1612.5, 22) * mm, "end": v(1612.5, 2280) * mm});
            skLineSegment(sketch, "E103.right", {"start": v(880.1, 22) * mm, "end": v(880.1, 1520) * mm});
            skLineSegment(sketch, "E104.bottom", {"start": v(880, 22) * mm, "end": v(-20, 22) * mm});
            skLineSegment(sketch, "E104.top", {"start": v(880, 2280) * mm, "end": v(-20, 2280) * mm});
            skLineSegment(sketch, "E104.left", {"start": v(880, 22) * mm, "end": v(880, 1520) * mm});
            skLineSegment(sketch, "E104.right", {"start": v(-20, 22) * mm, "end": v(-20, 2280) * mm});
            skLineSegment(sketch, "E105.bottom", {"start": v(208, 1925) * mm, "end": v(880, 1925) * mm});
            skLineSegment(sketch, "E105.top", {"start": v(208, 1520) * mm, "end": v(880, 1520) * mm});
            skLineSegment(sketch, "E105.left", {"start": v(208, 1925) * mm, "end": v(208, 1520) * mm});
            skLineSegment(sketch, "E105.right", {"start": v(1018, 1925) * mm, "end": v(1018, 1520) * mm});
            skLineSegment(sketch, "E106.trimOffspring", {"start": v(880, 1925) * mm, "end": v(880, 2280) * mm});
            skLineSegment(sketch, "E107.trimOffspring", {"start": v(880.1, 1925) * mm, "end": v(880.1, 2280) * mm});
            skLineSegment(sketch, "E108.trimOffspring", {"start": v(880.1, 1925) * mm, "end": v(1018, 1925) * mm});
            skLineSegment(sketch, "E109.trimOffspring", {"start": v(880.1, 1520) * mm, "end": v(1018, 1520) * mm});
            skLineSegment(sketch, "E110.bottom", {"start": v(1165, 2160) * mm, "end": v(1315, 2160) * mm});
            skLineSegment(sketch, "E110.top", {"start": v(1165, 2010) * mm, "end": v(1315, 2010) * mm});
            skLineSegment(sketch, "E110.left", {"start": v(1165, 2160) * mm, "end": v(1165, 2010) * mm});
            skLineSegment(sketch, "E110.right", {"start": v(1315, 2160) * mm, "end": v(1315, 2010) * mm});
            skSolve(sketch);
        }
        {
            var Q0;
            Q0 = qSketchRegion(id + "F41", true);
            extrude(context, id + "F42", {"entities" : qUnion([Q0]), "depth" : 12.5 * mm});
        }
        {
            var Q0;
            Q0=makeQuery(id+"F16.opExtrude","CAP_FACE",FACE,{"disambiguationData":[OSD([sQuery(id+"F15.wireOp",EDGE,"E36.bottom"),sQuery(id+"F15.wireOp",EDGE,"E36.top"),sQuery(id+"F15.wireOp",EDGE,"E36.left"),sQuery(id+"F15.wireOp",EDGE,"E36.right")])],"isStart":false});
            var sketch = newSketch(context, id + "F43", { "sketchPlane" : qUnion([Q0])});
            skLineSegment(sketch, "E111.bottom", {"start": v(579, 7) * mm, "end": v(1179, 7) * mm});
            skLineSegment(sketch, "E111.top", {"start": v(579, 2283) * mm, "end": v(1179, 2283) * mm});
            skLineSegment(sketch, "E111.left", {"start": v(579, 7) * mm, "end": v(579, 2283) * mm});
            skLineSegment(sketch, "E111.right", {"start": v(1179, 7) * mm, "end": v(1179, 2283) * mm});
            skLineSegment(sketch, "E112.bottom", {"start": v(1180, 2283) * mm, "end": v(1712, 2283) * mm});
            skLineSegment(sketch, "E112.top", {"start": v(1180, 7) * mm, "end": v(1712, 7) * mm});
            skLineSegment(sketch, "E112.left", {"start": v(1180, 2283) * mm, "end": v(1180, 7) * mm});
            skLineSegment(sketch, "E112.right", {"start": v(1712, 2283) * mm, "end": v(1712, 7) * mm});
            skLineSegment(sketch, "E113.bottom", {"start": v(578, 2101) * mm, "end": v(7, 2101) * mm});
            skLineSegment(sketch, "E113.top", {"start": v(578, 2283) * mm, "end": v(7, 2283) * mm});
            skLineSegment(sketch, "E113.left", {"start": v(578, 2101) * mm, "end": v(578, 2283) * mm});
            skLineSegment(sketch, "E113.right", {"start": v(7, 2101) * mm, "end": v(7, 2283) * mm});
            skLineSegment(sketch, "E114.bottom", {"start": v(7, 2100) * mm, "end": v(44, 2100) * mm});
            skLineSegment(sketch, "E114.top", {"start": v(7, 7) * mm, "end": v(44, 7) * mm});
            skLineSegment(sketch, "E114.left", {"start": v(7, 2100) * mm, "end": v(7, 7) * mm});
            skLineSegment(sketch, "E114.right", {"start": v(44, 2100) * mm, "end": v(44, 7) * mm});
            skSolve(sketch);
        }
        {
            var Q0;
            Q0 = qSketchRegion(id + "F43", true);
            extrude(context, id + "F44", {"entities" : qUnion([Q0]), "depth" : 12.5 * mm});
        }
        {
            var Q0;
            Q0=makeQuery(id+"F14.opExtrude","CAP_FACE",FACE,{"disambiguationData":[OSD([sQuery(id+"F13.wireOp",EDGE,"E23.bottom"),sQuery(id+"F13.wireOp",EDGE,"E23.top"),sQuery(id+"F13.wireOp",EDGE,"E23.left"),sQuery(id+"F13.wireOp",EDGE,"E23.right")])],"isStart":false});
            var sketch = newSketch(context, id + "F45", { "sketchPlane" : qUnion([Q0])});
            skLineSegment(sketch, "E115.bottom", {"start": v(-607, 2283) * mm, "end": v(-7, 2283) * mm});
            skLineSegment(sketch, "E115.top", {"start": v(-607, 7) * mm, "end": v(-7, 7) * mm});
            skLineSegment(sketch, "E115.left", {"start": v(-607, 2283) * mm, "end": v(-607, 7) * mm});
            skLineSegment(sketch, "E115.right", {"start": v(-7, 2283) * mm, "end": v(-7, 7) * mm});
            skLineSegment(sketch, "E116.1.0.0", {"start": v(-1208, 2283) * mm, "end": v(-1208, 7) * mm});
            skLineSegment(sketch, "E116.1.0.1", {"start": v(-1208, 2283) * mm, "end": v(-608, 2283) * mm});
            skLineSegment(sketch, "E116.1.0.2", {"start": v(-608, 2283) * mm, "end": v(-608, 7) * mm});
            skLineSegment(sketch, "E116.1.0.3", {"start": v(-1208, 7) * mm, "end": v(-608, 7) * mm});
            skLineSegment(sketch, "E116.2.0.0", {"start": v(-1809, 2283) * mm, "end": v(-1809, 7) * mm});
            skLineSegment(sketch, "E116.2.0.1", {"start": v(-1809, 2283) * mm, "end": v(-1209, 2283) * mm});
            skLineSegment(sketch, "E116.2.0.2", {"start": v(-1209, 2283) * mm, "end": v(-1209, 7) * mm});
            skLineSegment(sketch, "E116.2.0.3", {"start": v(-1809, 7) * mm, "end": v(-1209, 7) * mm});
            skLineSegment(sketch, "E116.direction1", {"start": v(-607, 7) * mm, "end": v(-1208, 7) * mm, "construction": true});
            skLineSegment(sketch, "E117.bottom", {"start": v(-1810, 2283) * mm, "end": v(-2084, 2283) * mm});
            skLineSegment(sketch, "E117.top", {"start": v(-1810, 7) * mm, "end": v(-2084, 7) * mm});
            skLineSegment(sketch, "E117.left", {"start": v(-1810, 2283) * mm, "end": v(-1810, 7) * mm});
            skLineSegment(sketch, "E117.right", {"start": v(-2084, 2283) * mm, "end": v(-2084, 7) * mm});
            skSolve(sketch);
        }
        {
            var Q0;
            Q0 = qSketchRegion(id + "F45", true);
            extrude(context, id + "F46", {"entities" : qUnion([Q0]), "depth" : 12.5 * mm});
        }
    });
